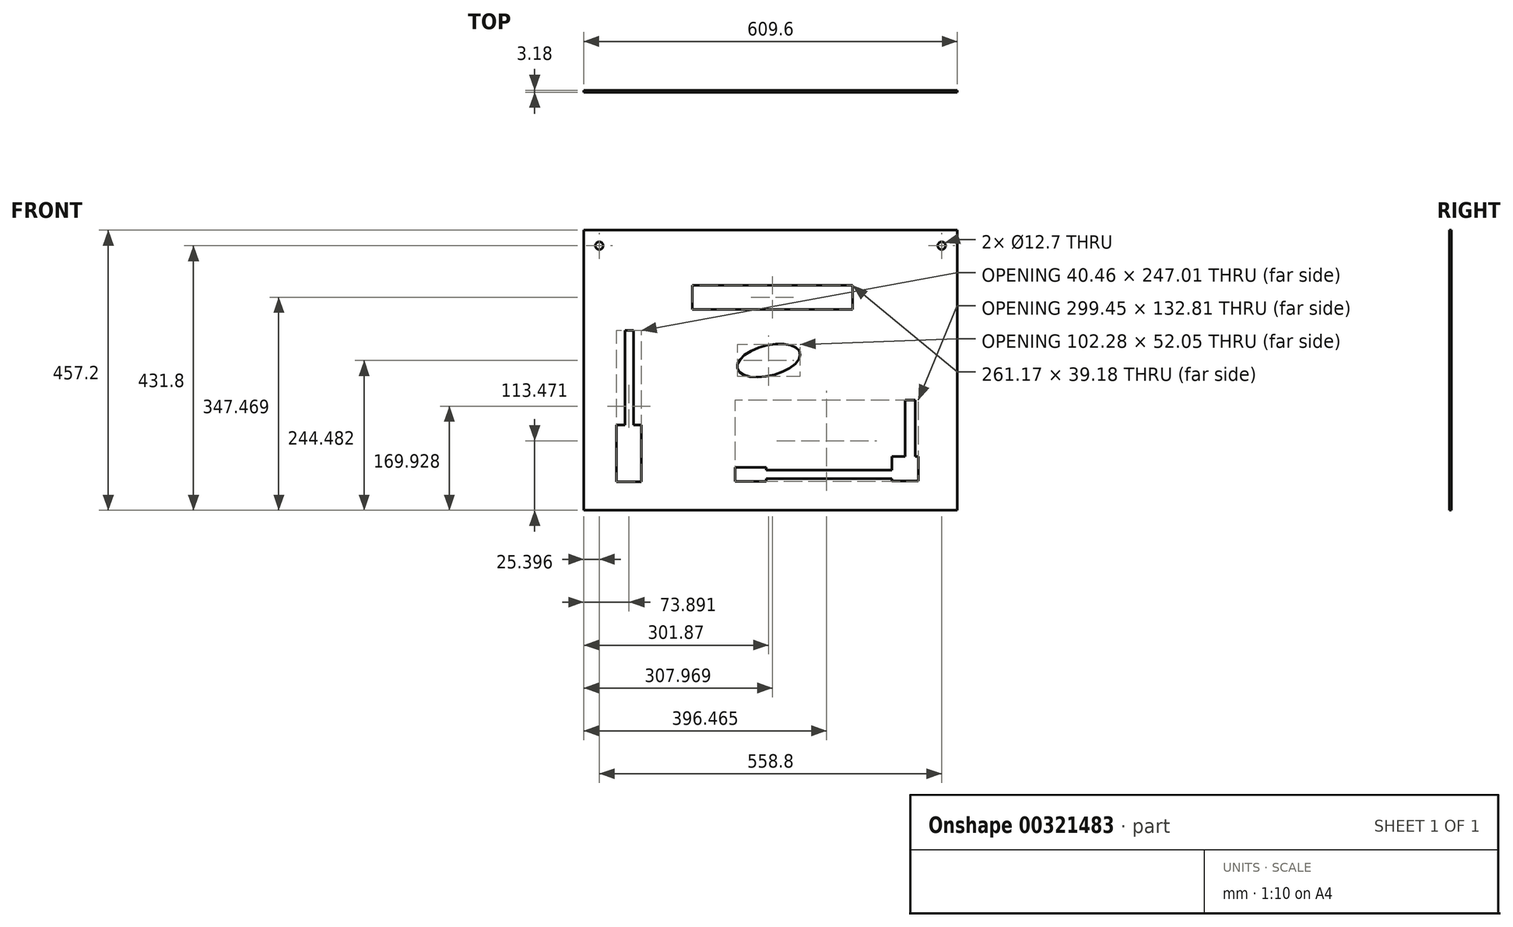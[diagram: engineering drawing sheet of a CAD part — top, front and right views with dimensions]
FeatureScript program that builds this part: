
annotation { "Feature Type Name" : "Feature", "Feature Type Description" : "" }
export const myFeature = defineFeature(function(context is Context, id is Id, definition is map)
    precondition{}
    {
        {
            var Q0;
            Q0=qCreatedBy(makeId("Front.planeOp"),FACE);
            var sketch = newSketch(context, id + "F0", { "sketchPlane" : qUnion([Q0])});
            skLineSegment(sketch, "E0.bottom", {"start": v(-301.87, 259.12) * mm, "end": v(307.73, 259.12) * mm});
            skLineSegment(sketch, "E0.top", {"start": v(-301.87, -198.08) * mm, "end": v(307.73, -198.08) * mm});
            skLineSegment(sketch, "E0.left", {"start": v(-301.87, 259.12) * mm, "end": v(-301.87, -198.08) * mm});
            skLineSegment(sketch, "E0.right", {"start": v(307.73, 259.12) * mm, "end": v(307.73, -198.08) * mm});
            skCircle(sketch, "E1", {"center": v(-276.47, 233.72) * mm, "radius": 6.35 * mm});
            skCircle(sketch, "E2", {"center": v(282.33, 233.72) * mm, "radius": 6.35 * mm});
            skLineSegment(sketch, "E3.bottom", {"start": v(-124.48, 168.98) * mm, "end": v(136.68, 168.98) * mm});
            skLineSegment(sketch, "E3.top", {"start": v(-124.48, 129.8) * mm, "end": v(136.68, 129.8) * mm});
            skLineSegment(sketch, "E3.left", {"start": v(-124.48, 168.98) * mm, "end": v(-124.48, 129.8) * mm});
            skLineSegment(sketch, "E3.right", {"start": v(136.68, 168.98) * mm, "end": v(136.68, 129.8) * mm});
            skLineSegment(sketch, "E4.bottom", {"start": v(-119.28, 164.01) * mm, "end": v(131.9, 164.01) * mm});
            skLineSegment(sketch, "E4.top", {"start": v(-119.28, 134.33) * mm, "end": v(131.9, 134.33) * mm});
            skLineSegment(sketch, "E4.left", {"start": v(-119.28, 164.01) * mm, "end": v(-119.28, 134.33) * mm});
            skLineSegment(sketch, "E4.right", {"start": v(131.9, 164.01) * mm, "end": v(131.9, 134.33) * mm});
            skEllipse(sketch, "E5", {"center": v(0, 46.4) * mm, "majorRadius": 52.7 * mm, "minorRadius": 24.82 * mm, "majorAxis": v(-0.97, -0.24)});
            skLineSegment(sketch, "E6.bottom", {"start": v(-234.37, 95.35) * mm, "end": v(-220.53, 95.35) * mm});
            skLineSegment(sketch, "E6.top", {"start": v(-234.37, -95.23) * mm, "end": v(-220.53, -95.23) * mm});
            skLineSegment(sketch, "E6.left", {"start": v(-234.37, 95.35) * mm, "end": v(-234.37, -95.23) * mm});
            skLineSegment(sketch, "E6.right", {"start": v(-220.53, 95.35) * mm, "end": v(-220.53, -95.23) * mm});
            skLineSegment(sketch, "E7.bottom", {"start": v(-207.75, -59.03) * mm, "end": v(-248.2, -59.03) * mm});
            skLineSegment(sketch, "E7.top", {"start": v(-207.75, -151.66) * mm, "end": v(-248.2, -151.66) * mm});
            skLineSegment(sketch, "E7.left", {"start": v(-207.75, -59.03) * mm, "end": v(-207.75, -151.66) * mm});
            skLineSegment(sketch, "E7.right", {"start": v(-248.2, -59.03) * mm, "end": v(-248.2, -151.66) * mm});
            skLineSegment(sketch, "E8.bottom", {"start": v(-20.7, -132.53) * mm, "end": v(218.75, -132.53) * mm});
            skLineSegment(sketch, "E8.top", {"start": v(-20.7, -146.37) * mm, "end": v(218.75, -146.37) * mm});
            skLineSegment(sketch, "E8.left", {"start": v(-20.7, -132.53) * mm, "end": v(-20.7, -146.37) * mm});
            skLineSegment(sketch, "E8.right", {"start": v(218.75, -132.53) * mm, "end": v(218.75, -146.37) * mm});
            skLineSegment(sketch, "E9.bottom", {"start": v(-4.24, -128.24) * mm, "end": v(-55.13, -128.24) * mm});
            skLineSegment(sketch, "E9.top", {"start": v(-4.24, -151.01) * mm, "end": v(-55.13, -151.01) * mm});
            skLineSegment(sketch, "E9.left", {"start": v(-4.24, -128.24) * mm, "end": v(-4.24, -151.01) * mm});
            skLineSegment(sketch, "E9.right", {"start": v(-55.13, -128.24) * mm, "end": v(-55.13, -151.01) * mm});
            skLineSegment(sketch, "E10.bottom", {"start": v(200.96, -150.04) * mm, "end": v(244.32, -150.04) * mm});
            skLineSegment(sketch, "E10.top", {"start": v(200.96, -110.18) * mm, "end": v(244.32, -110.18) * mm});
            skLineSegment(sketch, "E10.left", {"start": v(200.96, -150.04) * mm, "end": v(200.96, -110.18) * mm});
            skLineSegment(sketch, "E10.right", {"start": v(244.32, -150.04) * mm, "end": v(244.32, -110.18) * mm});
            skLineSegment(sketch, "E11.bottom", {"start": v(239.43, -130.1) * mm, "end": v(222.64, -130.1) * mm});
            skLineSegment(sketch, "E11.top", {"start": v(239.43, -18.2) * mm, "end": v(222.64, -18.2) * mm});
            skLineSegment(sketch, "E11.left", {"start": v(239.43, -130.1) * mm, "end": v(239.43, -18.2) * mm});
            skLineSegment(sketch, "E11.right", {"start": v(222.64, -130.1) * mm, "end": v(222.64, -18.2) * mm});
            skSolve(sketch);
        }
        {
            var Q0;
            Q0=makeQuery(id+"F0.imprint","IMPRINT",FACE,{"disambiguationData":[TD([[makeQuery(id+"F0.imprint","IMPRINT",EDGE,{"derivedFrom":sQuery(id+"F0.wireOp",EDGE,"E0.bottom")}),-1.0]])]});
            extrude(context, id + "F1", {"entities" : qUnion([Q0]), "depth" : 3.17 * mm});
        }
    });
